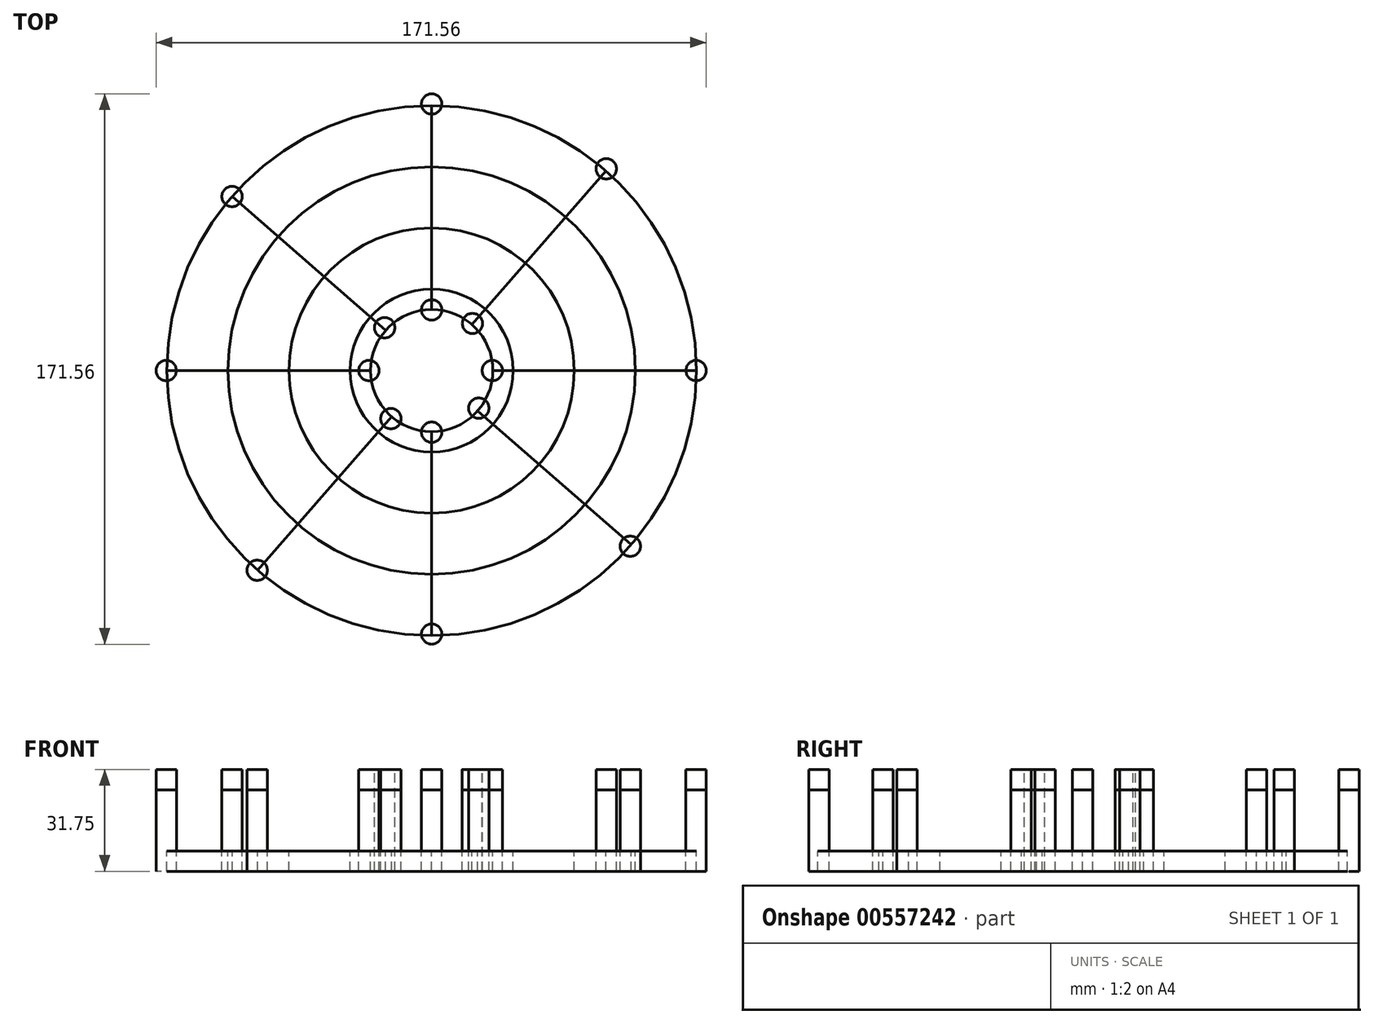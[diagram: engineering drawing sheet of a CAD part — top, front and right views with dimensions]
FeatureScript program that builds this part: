
annotation { "Feature Type Name" : "Feature", "Feature Type Description" : "" }
export const myFeature = defineFeature(function(context is Context, id is Id, definition is map)
    precondition{}
    {
        {
            var Q0;
            Q0=qCreatedBy(makeId("Top.planeOp"),FACE);
            var sketch = newSketch(context, id + "F0", { "sketchPlane" : qUnion([Q0])});
            skCircle(sketch, "E0", {"center": v(0, 0) * mm, "radius": 82.55 * mm});
            skCircle(sketch, "E1", {"center": v(0, 0) * mm, "radius": 19.05 * mm});
            skLineSegment(sketch, "E2", {"start": v(0, 19.05) * mm, "end": v(0, 82.55) * mm});
            skLineSegment(sketch, "E3", {"start": v(-82.55, 0) * mm, "end": v(-19.05, 0) * mm});
            skLineSegment(sketch, "E4", {"start": v(0, -19.05) * mm, "end": v(0, -82.55) * mm});
            skLineSegment(sketch, "E5", {"start": v(19.05, 0) * mm, "end": v(82.55, 0) * mm});
            skLineSegment(sketch, "E6", {"start": v(-14.35, 12.53) * mm, "end": v(-62.2, 54.28) * mm});
            skLineSegment(sketch, "E7", {"start": v(14.35, -12.53) * mm, "end": v(62.2, -54.28) * mm});
            skLineSegment(sketch, "E8", {"start": v(-12.53, -14.35) * mm, "end": v(-54.28, -62.2) * mm});
            skLineSegment(sketch, "E9", {"start": v(12.53, 14.35) * mm, "end": v(54.28, 62.2) * mm});
            skSolve(sketch);
        }
        {
            var Q0;
            Q0=sQuery(id+"F0.wireOp",EDGE,"E0");
            extrude(context, id + "F1", {"bodyType" : ToolBodyType.SURFACE, "surfaceEntities" : qUnion([Q0]), "depth" : 6.35 * mm, "offsetDistance" : 25.4 * mm});
        }
        {
            var Q0;
            Q0=sQuery(id+"F0.wireOp",EDGE,"E1");
            extrude(context, id + "F2", {"bodyType" : ToolBodyType.SURFACE, "surfaceEntities" : qUnion([Q0]), "depth" : 6.35 * mm, "offsetDistance" : 25.4 * mm});
        }
        {
            var Q0;
            Q0=sQuery(id+"F0.wireOp",EDGE,"E3");
            extrude(context, id + "F3", {"bodyType" : ToolBodyType.SURFACE, "surfaceEntities" : qUnion([Q0]), "depth" : 6.35 * mm, "offsetDistance" : 25.4 * mm});
        }
        {
            var Q0;
            Q0=sQuery(id+"F0.wireOp",EDGE,"E8");
            extrude(context, id + "F4", {"bodyType" : ToolBodyType.SURFACE, "surfaceEntities" : qUnion([Q0]), "depth" : 6.35 * mm, "offsetDistance" : 25.4 * mm});
        }
        {
            var Q0;
            Q0=sQuery(id+"F0.wireOp",EDGE,"E4");
            extrude(context, id + "F5", {"bodyType" : ToolBodyType.SURFACE, "surfaceEntities" : qUnion([Q0]), "depth" : 6.35 * mm, "offsetDistance" : 25.4 * mm});
        }
        {
            var Q0;
            Q0=sQuery(id+"F0.wireOp",EDGE,"E7");
            extrude(context, id + "F6", {"bodyType" : ToolBodyType.SURFACE, "surfaceEntities" : qUnion([Q0]), "depth" : 6.35 * mm, "offsetDistance" : 25.4 * mm});
        }
        {
            var Q0;
            Q0=sQuery(id+"F0.wireOp",EDGE,"E6");
            extrude(context, id + "F7", {"bodyType" : ToolBodyType.SURFACE, "surfaceEntities" : qUnion([Q0]), "depth" : 6.35 * mm, "offsetDistance" : 25.4 * mm});
        }
        {
            var Q0;
            Q0=sQuery(id+"F0.wireOp",EDGE,"E5");
            var Q1;
            Q1=sQuery(id+"F0.wireOp",EDGE,"E9");
            var Q2;
            Q2=sQuery(id+"F0.wireOp",EDGE,"E2");
            extrude(context, id + "F8", {"bodyType" : ToolBodyType.SURFACE, "surfaceEntities" : qUnion([Q0, Q1, Q2]), "depth" : 6.35 * mm, "offsetDistance" : 25.4 * mm});
        }
        {
            var Q0;
            Q0=qCreatedBy(makeId("Top.planeOp"),FACE);
            var sketch = newSketch(context, id + "F9", { "sketchPlane" : qUnion([Q0])});
            skCircle(sketch, "E10", {"center": v(-62.23, 54.26) * mm, "radius": 3.18 * mm});
            skCircle(sketch, "E11", {"center": v(-82.77, 0) * mm, "radius": 3.18 * mm});
            skCircle(sketch, "E12", {"center": v(-54.42, -62.24) * mm, "radius": 3.18 * mm});
            skCircle(sketch, "E13", {"center": v(0, -82.12) * mm, "radius": 3.18 * mm});
            skCircle(sketch, "E14", {"center": v(61.91, -54.74) * mm, "radius": 3.18 * mm});
            skCircle(sketch, "E15", {"center": v(82.44, 0) * mm, "radius": 3.18 * mm});
            skCircle(sketch, "E16", {"center": v(54.42, 62.9) * mm, "radius": 3.18 * mm});
            skCircle(sketch, "E17", {"center": v(0, 83.1) * mm, "radius": 3.17 * mm});
            skCircle(sketch, "E18", {"center": v(-19.55, 0) * mm, "radius": 3.18 * mm});
            skCircle(sketch, "E19", {"center": v(0, 18.9) * mm, "radius": 3.18 * mm});
            skCircle(sketch, "E20", {"center": v(-14.66, 13.36) * mm, "radius": 3.18 * mm});
            skCircle(sketch, "E21", {"center": v(-12.7, -14.99) * mm, "radius": 3.18 * mm});
            skCircle(sketch, "E22", {"center": v(0, -19.23) * mm, "radius": 3.18 * mm});
            skCircle(sketch, "E23", {"center": v(12.7, 14.66) * mm, "radius": 3.18 * mm});
            skCircle(sketch, "E24", {"center": v(18.9, 0) * mm, "radius": 3.18 * mm});
            skCircle(sketch, "E25", {"center": v(14.66, -11.73) * mm, "radius": 3.18 * mm});
            skSolve(sketch);
        }
        {
            var Q0;
            Q0=sQuery(id+"F9.wireOp",EDGE,"E10");
            var Q1;
            Q1=sQuery(id+"F9.wireOp",EDGE,"E11");
            var Q2;
            Q2=sQuery(id+"F9.wireOp",EDGE,"E12");
            var Q3;
            Q3=sQuery(id+"F9.wireOp",EDGE,"E13");
            var Q4;
            Q4=sQuery(id+"F9.wireOp",EDGE,"E14");
            var Q5;
            Q5=sQuery(id+"F9.wireOp",EDGE,"E15");
            var Q6;
            Q6=sQuery(id+"F9.wireOp",EDGE,"E16");
            var Q7;
            Q7=sQuery(id+"F9.wireOp",EDGE,"E17");
            var Q8;
            Q8=sQuery(id+"F9.wireOp",EDGE,"E20");
            var Q9;
            Q9=sQuery(id+"F9.wireOp",EDGE,"E19");
            var Q10;
            Q10=sQuery(id+"F9.wireOp",EDGE,"E23");
            var Q11;
            Q11=sQuery(id+"F9.wireOp",EDGE,"E24");
            var Q12;
            Q12=sQuery(id+"F9.wireOp",EDGE,"E25");
            var Q13;
            Q13=sQuery(id+"F9.wireOp",EDGE,"E22");
            var Q14;
            Q14=sQuery(id+"F9.wireOp",EDGE,"E21");
            var Q15;
            Q15=sQuery(id+"F9.wireOp",EDGE,"E18");
            extrude(context, id + "F10", {"bodyType" : ToolBodyType.SURFACE, "surfaceEntities" : qUnion([Q0, Q1, Q2, Q3, Q4, Q5, Q6, Q7, Q8, Q9, Q10, Q11, Q12, Q13, Q14, Q15]), "depth" : 31.75 * mm, "offsetDistance" : 25.4 * mm});
        }
        {
            var Q0;
            Q0=sQuery(id+"F9.wireOp",EDGE,"E17");
            var Q1;
            Q1=sQuery(id+"F9.wireOp",EDGE,"E16");
            var Q2;
            Q2=sQuery(id+"F9.wireOp",EDGE,"E15");
            var Q3;
            Q3=sQuery(id+"F9.wireOp",EDGE,"E14");
            var Q4;
            Q4=sQuery(id+"F9.wireOp",EDGE,"E13");
            var Q5;
            Q5=sQuery(id+"F9.wireOp",EDGE,"E12");
            var Q6;
            Q6=sQuery(id+"F9.wireOp",EDGE,"E11");
            var Q7;
            Q7=sQuery(id+"F9.wireOp",EDGE,"E10");
            var Q8;
            Q8=sQuery(id+"F9.wireOp",EDGE,"E20");
            var Q9;
            Q9=sQuery(id+"F9.wireOp",EDGE,"E18");
            var Q10;
            Q10=sQuery(id+"F9.wireOp",EDGE,"E21");
            var Q11;
            Q11=sQuery(id+"F9.wireOp",EDGE,"E22");
            var Q12;
            Q12=sQuery(id+"F9.wireOp",EDGE,"E25");
            var Q13;
            Q13=sQuery(id+"F9.wireOp",EDGE,"E24");
            var Q14;
            Q14=sQuery(id+"F9.wireOp",EDGE,"E23");
            var Q15;
            Q15=sQuery(id+"F9.wireOp",EDGE,"E19");
            extrude(context, id + "F11", {"bodyType" : ToolBodyType.SURFACE, "surfaceEntities" : qUnion([Q0, Q1, Q2, Q3, Q4, Q5, Q6, Q7, Q8, Q9, Q10, Q11, Q12, Q13, Q14, Q15]), "depth" : 25.4 * mm, "offsetDistance" : 25.4 * mm});
        }
        {
            var Q0;
            Q0=qCreatedBy(makeId("Top.planeOp"),FACE);
            var sketch = newSketch(context, id + "F12", { "sketchPlane" : qUnion([Q0])});
            skCircle(sketch, "E26", {"center": v(0, 0) * mm, "radius": 25.4 * mm});
            skCircle(sketch, "E27", {"center": v(0, 0) * mm, "radius": 44.45 * mm});
            skCircle(sketch, "E28", {"center": v(0, 0) * mm, "radius": 63.5 * mm});
            skSolve(sketch);
        }
        {
            var Q0;
            Q0=sQuery(id+"F12.wireOp",EDGE,"E28");
            var Q1;
            Q1=sQuery(id+"F12.wireOp",EDGE,"E27");
            var Q2;
            Q2=sQuery(id+"F12.wireOp",EDGE,"E26");
            extrude(context, id + "F13", {"bodyType" : ToolBodyType.SURFACE, "surfaceEntities" : qUnion([Q0, Q1, Q2]), "depth" : 6.35 * mm, "offsetDistance" : 25.4 * mm});
        }
    });
